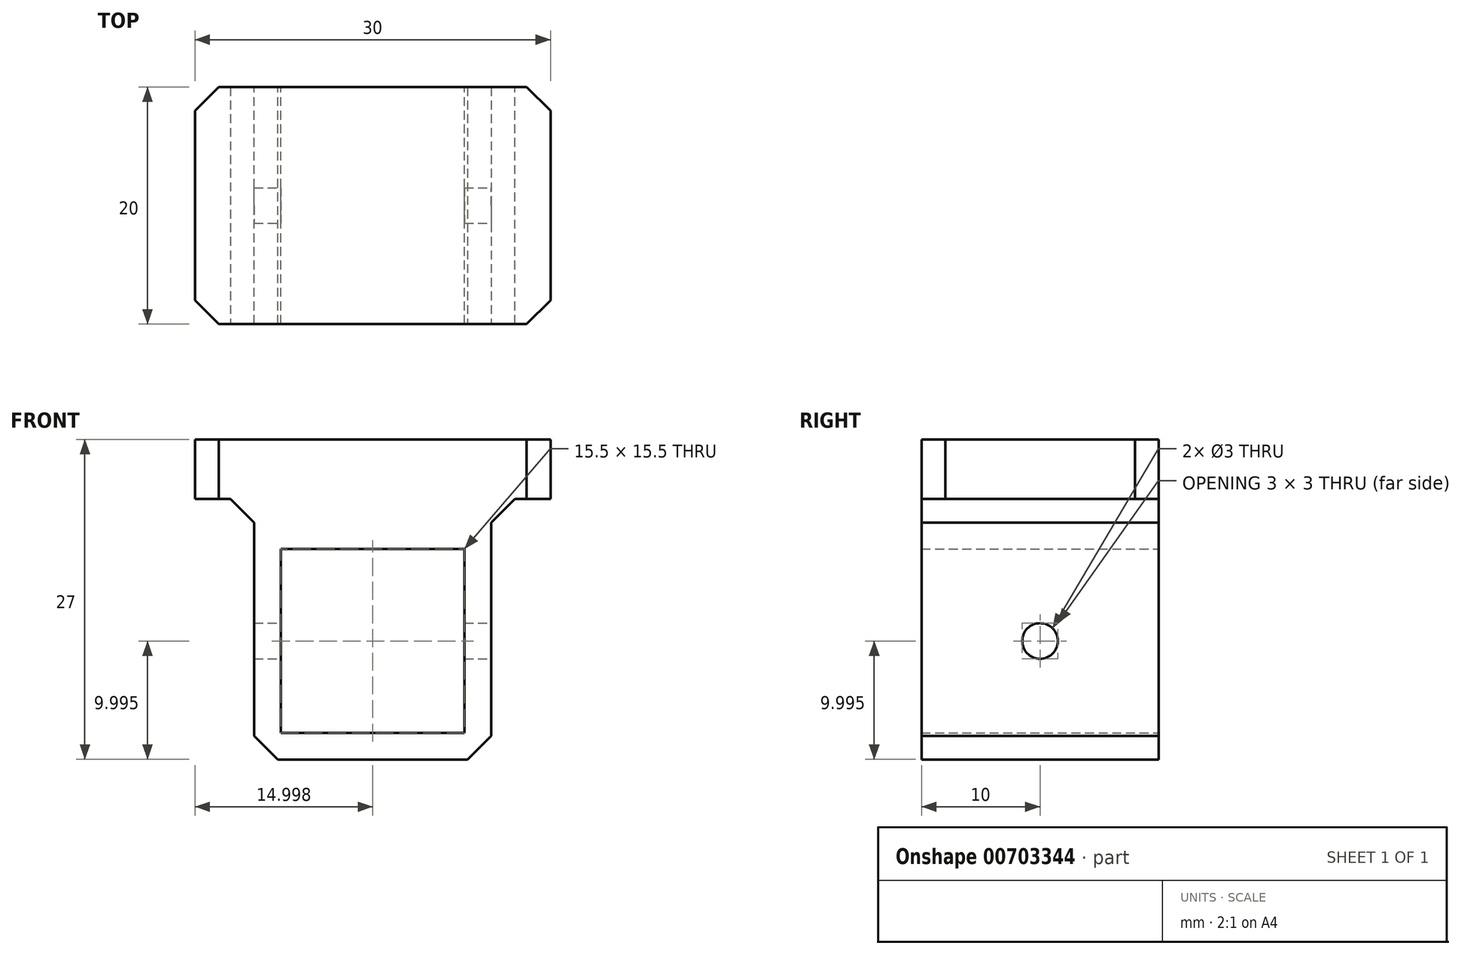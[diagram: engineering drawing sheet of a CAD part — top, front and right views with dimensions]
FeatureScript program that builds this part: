
annotation { "Feature Type Name" : "Feature", "Feature Type Description" : "" }
export const myFeature = defineFeature(function(context is Context, id is Id, definition is map)
    precondition{}
    {
        {
            var Q0;
            Q0=qCreatedBy(makeId("Front.planeOp"),FACE);
            var sketch = newSketch(context, id + "F0", { "sketchPlane" : qUnion([Q0])});
            skPoint(sketch, "E0.middle", {"position": v(-38.04, 18.75) * mm});
            skLineSegment(sketch, "E1.bottom", {"start": v(-28.04, 7.75) * mm, "end": v(-48.04, 7.75) * mm});
            skLineSegment(sketch, "E1.top", {"start": v(-28.04, 29.75) * mm, "end": v(-48.04, 29.75) * mm});
            skLineSegment(sketch, "E1.left", {"start": v(-28.04, 7.75) * mm, "end": v(-28.04, 29.75) * mm});
            skLineSegment(sketch, "E1.right", {"start": v(-48.04, 7.75) * mm, "end": v(-48.04, 29.75) * mm});
            skLineSegment(sketch, "E2", {"start": v(-48.04, 29.75) * mm, "end": v(-53.04, 29.75) * mm});
            skLineSegment(sketch, "E3", {"start": v(-53.04, 29.75) * mm, "end": v(-53.04, 34.75) * mm});
            skLineSegment(sketch, "E4", {"start": v(-53.04, 34.75) * mm, "end": v(-23.04, 34.75) * mm});
            skLineSegment(sketch, "E5", {"start": v(-23.04, 34.75) * mm, "end": v(-23.04, 29.75) * mm});
            skLineSegment(sketch, "E6", {"start": v(-23.04, 29.75) * mm, "end": v(-28.04, 29.75) * mm});
            skLineSegment(sketch, "E7.bottom", {"start": v(-30.3, 25.5) * mm, "end": v(-45.8, 25.5) * mm});
            skLineSegment(sketch, "E7.top", {"start": v(-30.3, 10) * mm, "end": v(-45.8, 10) * mm});
            skLineSegment(sketch, "E7.left", {"start": v(-30.3, 25.5) * mm, "end": v(-30.3, 10) * mm});
            skLineSegment(sketch, "E7.right", {"start": v(-45.8, 25.5) * mm, "end": v(-45.8, 10) * mm});
            skPoint(sketch, "E7.middle", {"position": v(-38.04, 17.75) * mm});
            skSolve(sketch);
        }
        {
            var Q0;
            Q0=makeQuery(id+"F0.imprint","IMPRINT",FACE,{"disambiguationData":[TD([[makeQuery(id+"F0.imprint","IMPRINT",EDGE,{"derivedFrom":sQuery(id+"F0.wireOp",EDGE,"E0.bottom")}),1.0]])]});
            var Q1;
            Q1=makeQuery(id+"F0.imprint","IMPRINT",FACE,{"disambiguationData":[TD([[makeQuery(id+"F0.imprint","IMPRINT",EDGE,{"derivedFrom":sQuery(id+"F0.wireOp",EDGE,"E1.bottom")}),-1.0]])]});
            var Q2;
            Q2=makeQuery(id+"F0.imprint","IMPRINT",FACE,{"disambiguationData":[TD([[makeQuery(id+"F0.imprint","IMPRINT",EDGE,{"derivedFrom":sQuery(id+"F0.wireOp",EDGE,"E1.top")}),-1.0]])]});
            extrude(context, id + "F1", {"entities" : qUnion([Q0, Q1, Q2]), "depth" : 20 * mm, "offsetDistance" : 25 * mm});
        }
        {
            var Q0;
            Q0=makeQuery(id+"F1.opExtrude","SWEPT_EDGE",EDGE,{"disambiguationData":[OSD([sQuery(id+"F0.wireOp",EDGE,"E1.bottom"),sQuery(id+"F0.wireOp",EDGE,"E1.left")])]});
            var Q1;
            Q1=makeQuery(id+"F1.opExtrude","SWEPT_EDGE",EDGE,{"disambiguationData":[OSD([sQuery(id+"F0.wireOp",EDGE,"E1.bottom"),sQuery(id+"F0.wireOp",EDGE,"E1.right")])]});
            var Q2;
            Q2=makeQuery(id+"F1.opExtrude","SWEPT_EDGE",EDGE,{"disambiguationData":[OSD([sQuery(id+"F0.wireOp",EDGE,"E1.top"),sQuery(id+"F0.wireOp",EDGE,"E1.right"),sQuery(id+"F0.wireOp",EDGE,"E2")])]});
            var Q3;
            Q3=makeQuery(id+"F1.opExtrude","SWEPT_EDGE",EDGE,{"disambiguationData":[OSD([sQuery(id+"F0.wireOp",EDGE,"E1.top"),sQuery(id+"F0.wireOp",EDGE,"E1.left"),sQuery(id+"F0.wireOp",EDGE,"E6")])]});
            var Q4;
            Q4=makeQuery(id+"F1.opExtrude","CAP_EDGE",EDGE,{"disambiguationData":[OSD([sQuery(id+"F0.wireOp",EDGE,"E5")])],"isStart":true});
            var Q5;
            Q5=makeQuery(id+"F1.opExtrude","CAP_EDGE",EDGE,{"disambiguationData":[OSD([sQuery(id+"F0.wireOp",EDGE,"E3")])],"isStart":true});
            var Q6;
            Q6=makeQuery(id+"F1.opExtrude","CAP_EDGE",EDGE,{"disambiguationData":[OSD([sQuery(id+"F0.wireOp",EDGE,"E3")])],"isStart":false});
            var Q7;
            Q7=makeQuery(id+"F1.opExtrude","CAP_EDGE",EDGE,{"disambiguationData":[OSD([sQuery(id+"F0.wireOp",EDGE,"E5")])],"isStart":false});
            chamfer(context, id + "F2", {"entities" : qUnion([Q0, Q1, Q2, Q3, Q4, Q5, Q6, Q7]), "width" : 2 * mm, "tangentPropagation" : true});
        }
        {
            var Q0;
            Q0=makeQuery(id+"F1.opExtrude","SWEPT_FACE",FACE,{"disambiguationData":[OSD([sQuery(id+"F0.wireOp",EDGE,"E7.right")])]});
            var sketch = newSketch(context, id + "F3", { "sketchPlane" : qUnion([Q0])});
            skLineSegment(sketch, "E8", {"start": v(0, 25.5) * mm, "end": v(-20, 10) * mm, "construction": true});
            skLineSegment(sketch, "E9", {"start": v(-20, 10) * mm, "end": v(-20, 25.5) * mm, "construction": true});
            skLineSegment(sketch, "E10", {"start": v(-20, 25.5) * mm, "end": v(0, 10) * mm, "construction": true});
            skCircle(sketch, "E11", {"center": v(-10, 17.75) * mm, "radius": 1.5 * mm});
            skSolve(sketch);
        }
        {
            var Q0;
            Q0=makeQuery(id+"F3.imprint","IMPRINT",FACE,{"disambiguationData":[TD([[makeQuery(id+"F3.imprint","IMPRINT",EDGE,{"derivedFrom":sQuery(id+"F3.wireOp",EDGE,"E11")}),1.0]])]});
            extrude(context, id + "F4", {"entities" : qUnion([Q0]), "operationType" : NewBodyOperationType.REMOVE, "endBound" : BoundingType.THROUGH_ALL, "oppositeDirection" : true, "depth" : 25 * mm, "offsetDistance" : 25 * mm, "hasSecondDirection" : true, "secondDirectionOppositeDirection" : false, "secondDirectionDepth" : 25 * mm});
        }
    });
